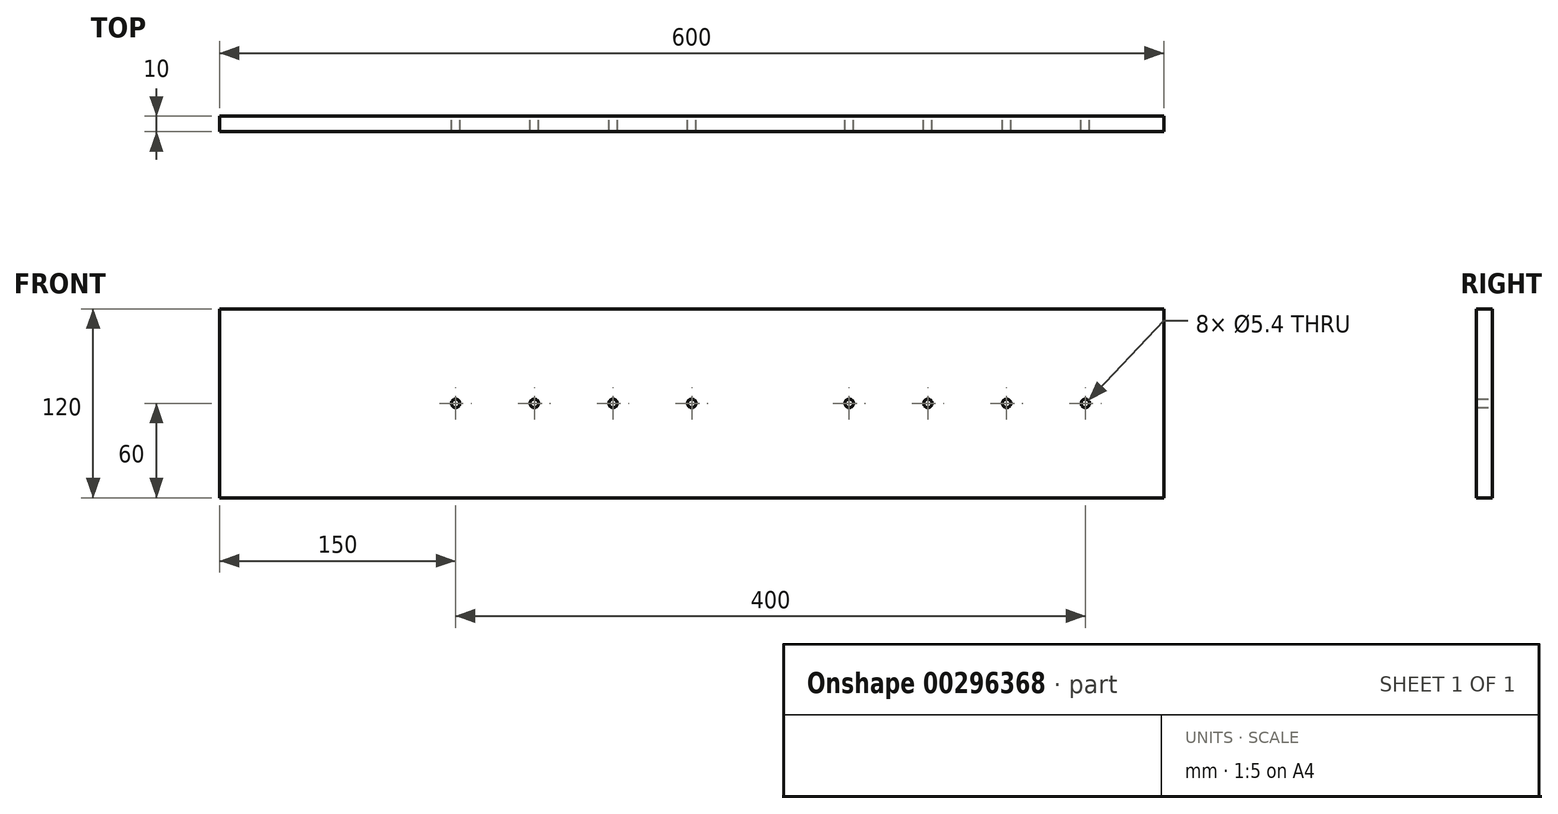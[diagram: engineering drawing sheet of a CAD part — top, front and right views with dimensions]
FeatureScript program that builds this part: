
annotation { "Feature Type Name" : "Feature", "Feature Type Description" : "" }
export const myFeature = defineFeature(function(context is Context, id is Id, definition is map)
    precondition{}
    {
        {
            var Q0;
            Q0=qCreatedBy(makeId("Front.planeOp"),FACE);
            var sketch = newSketch(context, id + "F0", { "sketchPlane" : qUnion([Q0])});
            skLineSegment(sketch, "E0.bottom", {"start": v(300, 60) * mm, "end": v(-300, 60) * mm});
            skLineSegment(sketch, "E0.top", {"start": v(300, -60) * mm, "end": v(-300, -60) * mm});
            skLineSegment(sketch, "E0.left", {"start": v(300, 60) * mm, "end": v(300, -60) * mm});
            skLineSegment(sketch, "E0.right", {"start": v(-300, 60) * mm, "end": v(-300, -60) * mm});
            skPoint(sketch, "E0.middle", {"position": v(0, 0) * mm});
            skLineSegment(sketch, "E1", {"start": v(-300, 0) * mm, "end": v(300, 0) * mm, "construction": true});
            skPoint(sketch, "E2", {"position": v(250, 0) * mm});
            skPoint(sketch, "E3.1.0.0", {"position": v(200, 0) * mm});
            skPoint(sketch, "E3.2.0.0", {"position": v(150, 0) * mm});
            skPoint(sketch, "E3.3.0.0", {"position": v(100, 0) * mm});
            skPoint(sketch, "E3.4.0.0", {"position": v(50, 0) * mm});
            skPoint(sketch, "E3.6.0.0", {"position": v(-50, 0) * mm});
            skPoint(sketch, "E3.7.0.0", {"position": v(-100, 0) * mm});
            skLineSegment(sketch, "E3.direction1", {"start": v(250, 0) * mm, "end": v(200, 0) * mm, "construction": true});
            skPoint(sketch, "E4.0.8.0", {"position": v(-150, 0) * mm});
            skSolve(sketch);
        }
        {
            var Q0;
            Q0 = qSketchRegion(id + "F0", true);
            extrude(context, id + "F1", {"entities" : qUnion([Q0]), "depth" : 10 * mm});
        }
        {
            var Q0;
            Q0=sQuery(id+"F0.wireOp",VERTEX,"E2");
            var Q1;
            Q1=sQuery(id+"F0.wireOp",VERTEX,"E3.1.0.0");
            var Q2;
            Q2=sQuery(id+"F0.wireOp",VERTEX,"E3.2.0.0");
            var Q3;
            Q3=sQuery(id+"F0.wireOp",VERTEX,"E3.3.0.0");
            var Q4;
            Q4=sQuery(id+"F0.wireOp",VERTEX,"E0.middle");
            var Q5;
            Q5=sQuery(id+"F0.wireOp",VERTEX,"E0.middle");
            var Q6;
            Q6=sQuery(id+"F0.wireOp",VERTEX,"E3.6.0.0");
            var Q7;
            Q7=sQuery(id+"F0.wireOp",VERTEX,"E3.7.0.0");
            var Q8;
            Q8=sQuery(id+"F0.wireOp",VERTEX,"E4.0.8.0");
            var Q9;
            Q9=makeQuery(id+"F1.opExtrude","SWEPT_BODY",BODY,{"disambiguationData":[OSD([sQuery(id+"F0.wireOp",EDGE,"E0.bottom"),sQuery(id+"F0.wireOp",EDGE,"E0.top"),sQuery(id+"F0.wireOp",EDGE,"E0.left"),sQuery(id+"F0.wireOp",EDGE,"E0.right")])]});
            hole(context, id + "F2", {"style" : HoleStyle.SIMPLE, "endStyle" : HoleEndStyle.THROUGH, "oppositeDirection" : true, "standardTappedOrClearance" : lookupTablePath({ "standard" : "ISO", "engagement" : "25%", "pitch" : "1 mm", "size" : "M6", "type" : "Tapped" }), "standardBlindInLast" : lookupTablePath({ "standard" : "ISO", "engagement" : "25%", "pitch" : "1 mm", "size" : "M6", "type" : "Tapped" }), "holeDiameter" : 5.4 * mm, "showTappedDepth" : true, "tappedDepth" : 8 * mm, "tapClearance" : 3, "locations" : qUnion([Q0, Q1, Q2, Q3, Q4, Q5, Q6, Q7, Q8]), "scope" : qUnion([Q9])});
        }
    });
